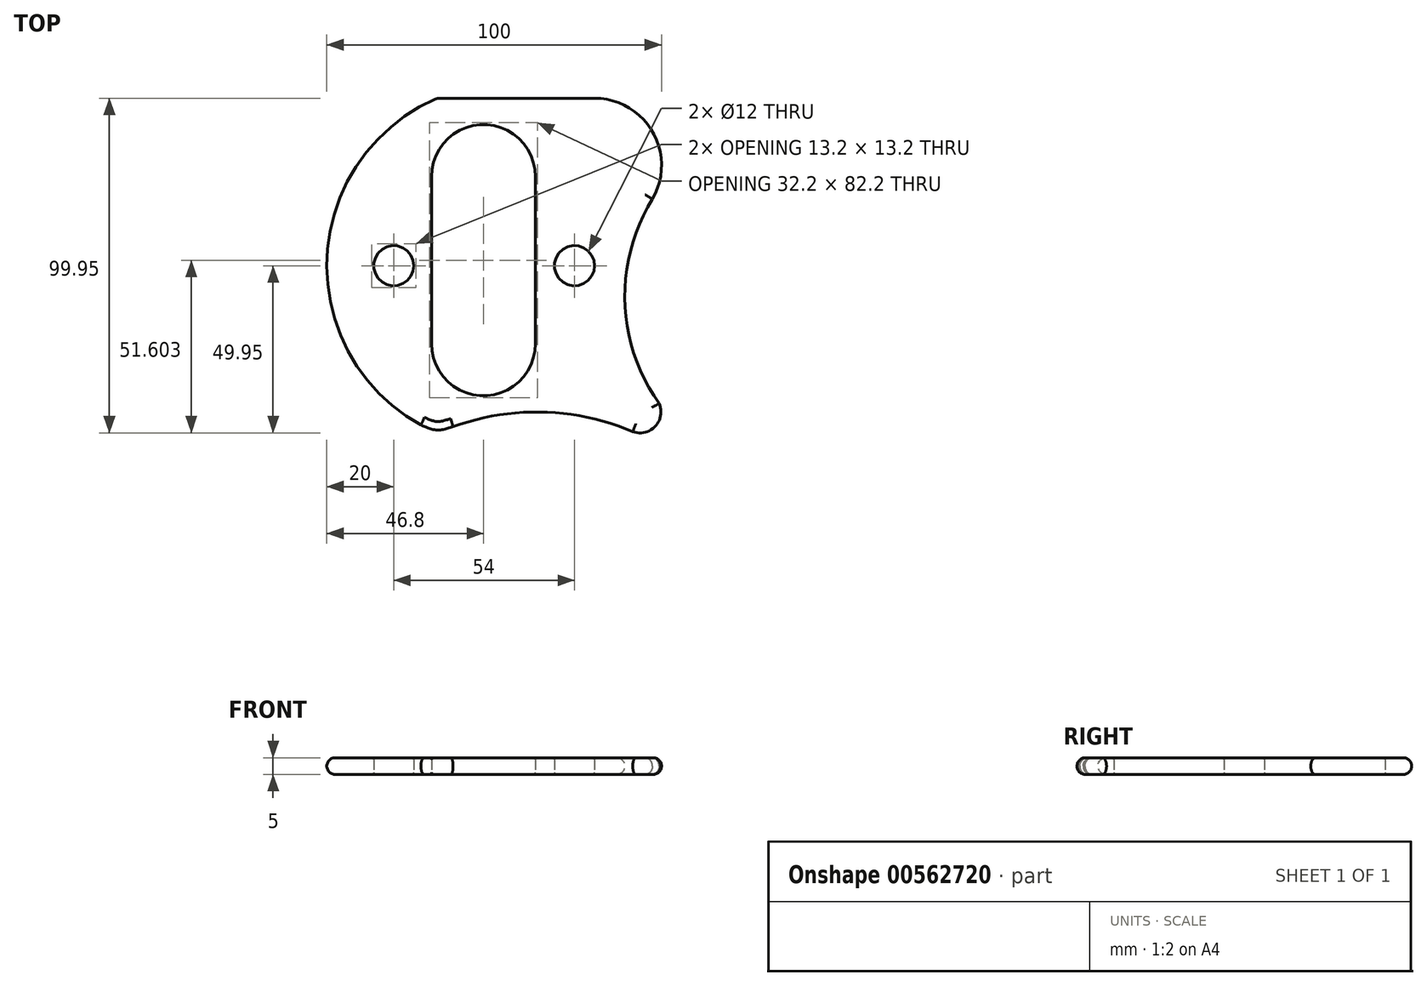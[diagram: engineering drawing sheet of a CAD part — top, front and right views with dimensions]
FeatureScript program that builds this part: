
annotation { "Feature Type Name" : "Feature", "Feature Type Description" : "" }
export const myFeature = defineFeature(function(context is Context, id is Id, definition is map)
    precondition{}
    {
        {
            var Q0;
            Q0=qCreatedBy(makeId("Top.planeOp"),FACE);
            var sketch = newSketch(context, id + "F0", { "sketchPlane" : qUnion([Q0])});
            skLineSegment(sketch, "E0.bottom", {"start": v(-17, 50) * mm, "end": v(30, 50) * mm});
            skPoint(sketch, "E0.middle", {"position": v(0, 0) * mm});
            skArc(sketch, "E1", {"start": v(-17, 50) * mm, "mid": v(-49.93, 2.72) * mm, "end": v(-21.9, -47.61) * mm});
            skPoint(sketch, "E1.second.point", {"position": v(-50, 0) * mm});
            skPoint(sketch, "E2.third.point", {"position": v(48.04, -39.34) * mm});
            skArc(sketch, "E3", {"start": v(42.4, -50) * mm, "mid": v(15.24, -43.74) * mm, "end": v(-12.27, -48.1) * mm});
            skPoint(sketch, "E3.second.point", {"position": v(13.98, -43.7) * mm});
            skPoint(sketch, "E3.third.point", {"position": v(40.9, -49.35) * mm});
            skArc(sketch, "E4.trimOffspring", {"start": v(40.9, -49.35) * mm, "mid": v(48.66, -47.33) * mm, "end": v(48.04, -39.34) * mm});
            skArc(sketch, "E5.trimOffspring", {"start": v(46.9, 19.3) * mm, "mid": v(47.52, 39.64) * mm, "end": v(30, 50) * mm});
            skCircle(sketch, "E6", {"center": v(-30, 0) * mm, "radius": 6 * mm});
            skCircle(sketch, "E7.MirrorC", {"center": v(24, 0) * mm, "radius": 6 * mm});
            skArc(sketch, "E8", {"start": v(47.27, 19.91) * mm, "mid": v(39.08, -11.54) * mm, "end": v(50, -42.14) * mm});
            skPoint(sketch, "E8.second.point", {"position": v(39.78, 0) * mm});
            skPoint(sketch, "E9.orphan", {"position": v(50, -50) * mm});
            skFitSpline(sketch, "E10", {"points": [v(-21.9, -47.61) * mm, v(-17.04, -49.1) * mm, v(-12.27, -48.1) * mm], "startDerivative": vector(9.45, -3.38) * mm, "endDerivative": vector(9.77, 2.25) * mm});
            skLineSegment(sketch, "E11", {"start": v(-3.2, 26.65) * mm, "end": v(-3.2, -23.35) * mm, "construction": true});
            skArc(sketch, "E12", {"start": v(12.3, 26.65) * mm, "mid": v(-3.2, 42.15) * mm, "end": v(-18.7, 26.65) * mm});
            skArc(sketch, "E13", {"start": v(-18.7, -23.35) * mm, "mid": v(-3.2, -38.85) * mm, "end": v(12.3, -23.35) * mm});
            skLineSegment(sketch, "E14", {"start": v(-30.34, 26.65) * mm, "end": v(29.4, 26.65) * mm, "construction": true});
            skLineSegment(sketch, "E15", {"start": v(-30, -23.35) * mm, "end": v(22.61, -23.35) * mm, "construction": true});
            skLineSegment(sketch, "E16", {"start": v(-18.7, 26.65) * mm, "end": v(-18.7, -23.35) * mm});
            skLineSegment(sketch, "E17", {"start": v(12.3, -23.35) * mm, "end": v(12.3, 26.65) * mm});
            skSolve(sketch);
        }
        {
            var Q0;
            {var subQ1=sQuery(id+"F0.wireOp",EDGE,"E0.bottom");Q0=makeQuery(id+"F0.imprint","IMPRINT",FACE,{"disambiguationData":[TD([[makeQuery(id+"F0.imprint","IMPRINT",EDGE,{"derivedFrom":subQ1}),-1.0]])]});}
            extrude(context, id + "F1", {"entities" : qUnion([Q0]), "depth" : 5 * mm, "offsetDistance" : 25 * mm});
        }
        {
            var Q0;
            Q0=makeQuery(id+"F1.opExtrude","SWEPT_EDGE",EDGE,{"disambiguationData":[OSD([sQuery(id+"F0.wireOp",EDGE,"E0.bottom"),sQuery(id+"F0.wireOp",EDGE,"E1")])]});
            fillet(context, id + "F2", {"entities" : qUnion([Q0]), "radius" : 3.1 * mm, "tangentPropagation" : true, "allowEdgeOverflow" : false});
        }
        {
            var Q0;
            Q0=makeQuery(id+"F1.opExtrude","CAP_EDGE",EDGE,{"disambiguationData":[OSD([sQuery(id+"F0.wireOp",EDGE,"E10")])],"isStart":false});
            var Q1;
            Q1=makeQuery(id+"F1.opExtrude","CAP_EDGE",EDGE,{"disambiguationData":[OSD([sQuery(id+"F0.wireOp",EDGE,"E3")])],"isStart":false});
            var Q2;
            Q2=makeQuery(id+"F1.opExtrude","CAP_EDGE",EDGE,{"disambiguationData":[OSD([sQuery(id+"F0.wireOp",EDGE,"E1")])],"isStart":false});
            var Q3;
            Q3=makeQuery(id+"F1.opExtrude","CAP_EDGE",EDGE,{"disambiguationData":[OSD([sQuery(id+"F0.wireOp",EDGE,"E1")])],"isStart":true});
            var Q4;
            Q4=makeQuery(id+"F1.opExtrude","CAP_EDGE",EDGE,{"disambiguationData":[OSD([sQuery(id+"F0.wireOp",EDGE,"E3")])],"isStart":true});
            var Q5;
            Q5=makeQuery(id+"F1.opExtrude","CAP_EDGE",EDGE,{"disambiguationData":[OSD([sQuery(id+"F0.wireOp",EDGE,"E10")])],"isStart":true});
            var Q6;
            Q6=makeQuery(id+"F1.opExtrude","CAP_EDGE",EDGE,{"disambiguationData":[OSD([sQuery(id+"F0.wireOp",EDGE,"E8")])],"isStart":false});
            var Q7;
            Q7=makeQuery(id+"F1.opExtrude","CAP_EDGE",EDGE,{"disambiguationData":[OSD([sQuery(id+"F0.wireOp",EDGE,"E8")])],"isStart":true});
            var Q8;
            Q8=makeQuery(id+"F1.opExtrude","CAP_EDGE",EDGE,{"disambiguationData":[OSD([sQuery(id+"F0.wireOp",EDGE,"E0.bottom")])],"isStart":false});
            var Q9;
            Q9=makeQuery(id+"F1.opExtrude","CAP_EDGE",EDGE,{"disambiguationData":[OSD([sQuery(id+"F0.wireOp",EDGE,"E0.bottom")])],"isStart":true});
            var Q10;
            Q10=makeQuery(id+"F1.opExtrude","CAP_EDGE",EDGE,{"disambiguationData":[OSD([sQuery(id+"F0.wireOp",EDGE,"E5.trimOffspring")])],"isStart":false});
            var Q11;
            Q11=makeQuery(id+"F1.opExtrude","CAP_EDGE",EDGE,{"disambiguationData":[OSD([sQuery(id+"F0.wireOp",EDGE,"E5.trimOffspring")])],"isStart":true});
            var Q12;
            Q12=makeQuery(id+"F1.opExtrude","CAP_EDGE",EDGE,{"disambiguationData":[OSD([sQuery(id+"F0.wireOp",EDGE,"E4.trimOffspring")])],"isStart":false});
            var Q13;
            Q13=makeQuery(id+"F1.opExtrude","CAP_EDGE",EDGE,{"disambiguationData":[OSD([sQuery(id+"F0.wireOp",EDGE,"E4.trimOffspring")])],"isStart":true});
            fillet(context, id + "F3", {"entities" : qUnion([Q0, Q1, Q2, Q3, Q4, Q5, Q6, Q7, Q8, Q9, Q10, Q11, Q12, Q13]), "radius" : 2.5 * mm, "allowEdgeOverflow" : false});
        }
        {
            var Q0;
            Q0=makeQuery(id+"F1.opExtrude","CAP_EDGE",EDGE,{"disambiguationData":[OSD([sQuery(id+"F0.wireOp",EDGE,"E17")])],"isStart":false});
            var Q1;
            Q1=makeQuery(id+"F1.opExtrude","CAP_EDGE",EDGE,{"disambiguationData":[OSD([sQuery(id+"F0.wireOp",EDGE,"E12")])],"isStart":true});
            var Q2;
            Q2=makeQuery(id+"F1.opExtrude","CAP_EDGE",EDGE,{"disambiguationData":[OSD([sQuery(id+"F0.wireOp",EDGE,"E6")])],"isStart":false});
            var Q3;
            Q3=makeQuery(id+"F1.opExtrude","CAP_EDGE",EDGE,{"disambiguationData":[OSD([sQuery(id+"F0.wireOp",EDGE,"E7.MirrorC")])],"isStart":false});
            var Q4;
            Q4=makeQuery(id+"F1.opExtrude","CAP_EDGE",EDGE,{"disambiguationData":[OSD([sQuery(id+"F0.wireOp",EDGE,"E7.MirrorC")])],"isStart":true});
            var Q5;
            Q5=makeQuery(id+"F1.opExtrude","CAP_EDGE",EDGE,{"disambiguationData":[OSD([sQuery(id+"F0.wireOp",EDGE,"E6")])],"isStart":true});
            fillet(context, id + "F4", {"entities" : qUnion([Q0, Q1, Q2, Q3, Q4, Q5]), "radius" : .6 * mm, "tangentPropagation" : true, "rho" : 0.5, "crossSection" : FilletCrossSection.CONIC, "allowEdgeOverflow" : false});
        }
    });
